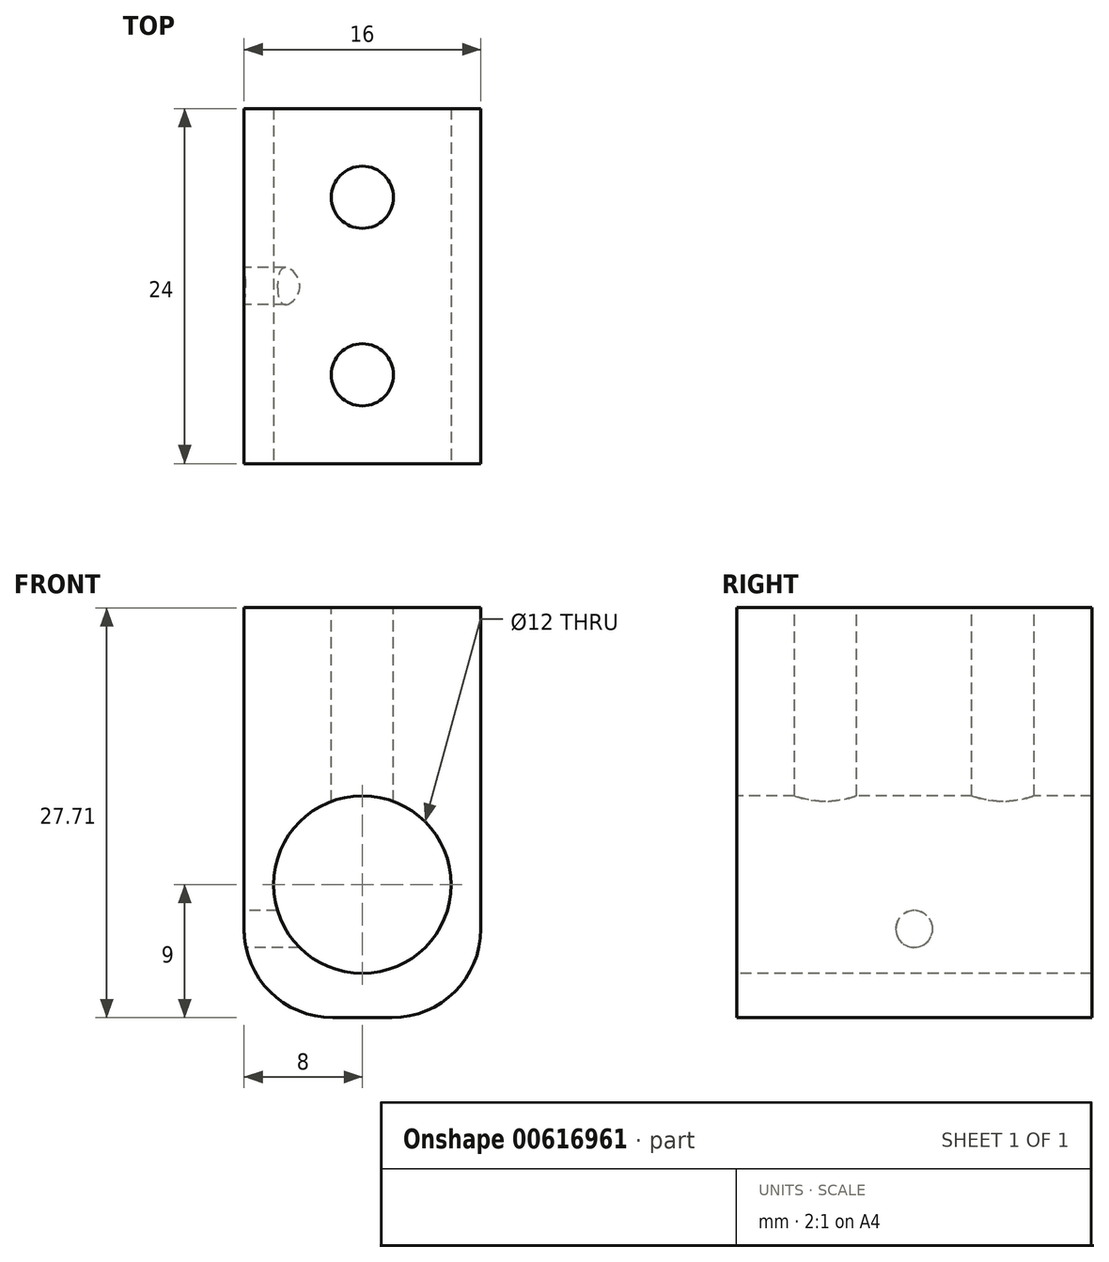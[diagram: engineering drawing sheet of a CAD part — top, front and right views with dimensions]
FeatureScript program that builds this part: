
annotation { "Feature Type Name" : "Feature", "Feature Type Description" : "" }
export const myFeature = defineFeature(function(context is Context, id is Id, definition is map)
    precondition{}
    {
        {
            var Q0;
            Q0=qCreatedBy(makeId("Front.planeOp"),FACE);
            var sketch = newSketch(context, id + "F0", { "sketchPlane" : qUnion([Q0])});
            skLineSegment(sketch, "E0.bottom", {"start": v(-8, 12.71) * mm, "end": v(8, 12.71) * mm});
            skLineSegment(sketch, "E0.top", {"start": v(-2, -15) * mm, "end": v(2, -15) * mm});
            skLineSegment(sketch, "E0.left", {"start": v(-8, 12.71) * mm, "end": v(-8, -9) * mm});
            skLineSegment(sketch, "E0.right", {"start": v(8, 12.71) * mm, "end": v(8, -9) * mm});
            skPoint(sketch, "E1", {"position": v(0, -6) * mm});
            skCircle(sketch, "E2", {"center": v(0, -6) * mm, "radius": 6 * mm});
            skPoint(sketch, "E3.visualSharp", {"position": v(8, -15) * mm});
            skArc(sketch, "E3.filletArc", {"start": v(2, -15) * mm, "mid": v(6.24, -13.24) * mm, "end": v(8, -9) * mm});
            skPoint(sketch, "E4.visualSharp", {"position": v(-8, -15) * mm});
            skArc(sketch, "E4.filletArc", {"start": v(-8, -9) * mm, "mid": v(-6.24, -13.24) * mm, "end": v(-2, -15) * mm});
            skSolve(sketch);
        }
        {
            var Q0;
            Q0=makeQuery(id+"F0.imprint","IMPRINT",FACE,{"disambiguationData":[TD([[makeQuery(id+"F0.imprint","IMPRINT",EDGE,{"derivedFrom":sQuery(id+"F0.wireOp",EDGE,"E0.bottom")}),-1.0]])]});
            extrude(context, id + "F1", {"entities" : qUnion([Q0]), "oppositeDirection" : true, "depth" : 24 * mm, "offsetDistance" : 25 * mm});
        }
        {
            var Q0;
            Q0=makeQuery(id+"F1.opExtrude","SWEPT_FACE",FACE,{"disambiguationData":[OSD([sQuery(id+"F0.wireOp",EDGE,"E0.bottom")])]});
            var sketch = newSketch(context, id + "F2", { "sketchPlane" : qUnion([Q0])});
            skPoint(sketch, "E5", {"position": v(0, 6) * mm});
            skPoint(sketch, "E6", {"position": v(0, 18) * mm});
            skSolve(sketch);
        }
        {
            var Q0;
            Q0=sQuery(id+"F2.wireOp",VERTEX,"E6");
            var Q1;
            Q1=sQuery(id+"F2.wireOp",VERTEX,"E5");
            var Q2;
            Q2=makeQuery(id+"F1.opExtrude","SWEPT_BODY",BODY,{"disambiguationData":[OSD([sQuery(id+"F0.wireOp",EDGE,"E0.bottom"),sQuery(id+"F0.wireOp",EDGE,"E0.top"),sQuery(id+"F0.wireOp",EDGE,"E0.left"),sQuery(id+"F0.wireOp",EDGE,"E0.right"),sQuery(id+"F0.wireOp",EDGE,"E2"),sQuery(id+"F0.wireOp",EDGE,"E3.filletArc"),sQuery(id+"F0.wireOp",EDGE,"E4.filletArc")])]});
            hole(context, id + "F3", {"style" : HoleStyle.SIMPLE, "endStyle" : HoleEndStyle.BLIND, "standardTappedOrClearance" : lookupTablePath({ "standard" : "ISO", "engagement" : "75%", "pitch" : "0.8 mm", "size" : "M5", "type" : "Tapped" }), "standardBlindInLast" : lookupTablePath({ "standard" : "ISO", "engagement" : "75%", "pitch" : "0.8 mm", "size" : "M5", "type" : "Tapped" }), "holeDiameter" : 4.2 * mm, "majorDiameter" : 5 * mm, "showTappedDepth" : true, "holeDepth" : 14.4 * mm, "isTappedThrough" : true, "tappedDepth" : 12 * mm, "tapClearance" : 3, "locations" : qUnion([Q0, Q1]), "scope" : qUnion([Q2])});
        }
        {
            var Q0;
            Q0=makeQuery(id+"F1.opExtrude","SWEPT_FACE",FACE,{"disambiguationData":[OSD([sQuery(id+"F0.wireOp",EDGE,"E0.left")])]});
            var sketch = newSketch(context, id + "F4", { "sketchPlane" : qUnion([Q0])});
            skPoint(sketch, "E7", {"position": v(-12, -9) * mm});
            skSolve(sketch);
        }
        {
            var Q0;
            Q0=sQuery(id+"F4.wireOp",VERTEX,"E7");
            var Q1;
            Q1=makeQuery(id+"F1.opExtrude","SWEPT_BODY",BODY,{"disambiguationData":[OSD([sQuery(id+"F0.wireOp",EDGE,"E0.bottom"),sQuery(id+"F0.wireOp",EDGE,"E0.top"),sQuery(id+"F0.wireOp",EDGE,"E0.left"),sQuery(id+"F0.wireOp",EDGE,"E0.right"),sQuery(id+"F0.wireOp",EDGE,"E2"),sQuery(id+"F0.wireOp",EDGE,"E3.filletArc"),sQuery(id+"F0.wireOp",EDGE,"E4.filletArc")])]});
            hole(context, id + "F5", {"style" : HoleStyle.SIMPLE, "endStyle" : HoleEndStyle.BLIND, "standardTappedOrClearance" : lookupTablePath({ "standard" : "ISO", "engagement" : "75%", "pitch" : "0.5 mm", "size" : "M3", "type" : "Tapped" }), "standardBlindInLast" : lookupTablePath({ "standard" : "ISO", "engagement" : "75%", "pitch" : "0.5 mm", "size" : "M3", "type" : "Tapped" }), "holeDiameter" : 2.5 * mm, "majorDiameter" : 3 * mm, "showTappedDepth" : true, "holeDepth" : 5 * mm, "isTappedThrough" : true, "tappedDepth" : 5 * mm, "tapClearance" : 0, "locations" : qUnion([Q0]), "scope" : qUnion([Q1])});
        }
    });
